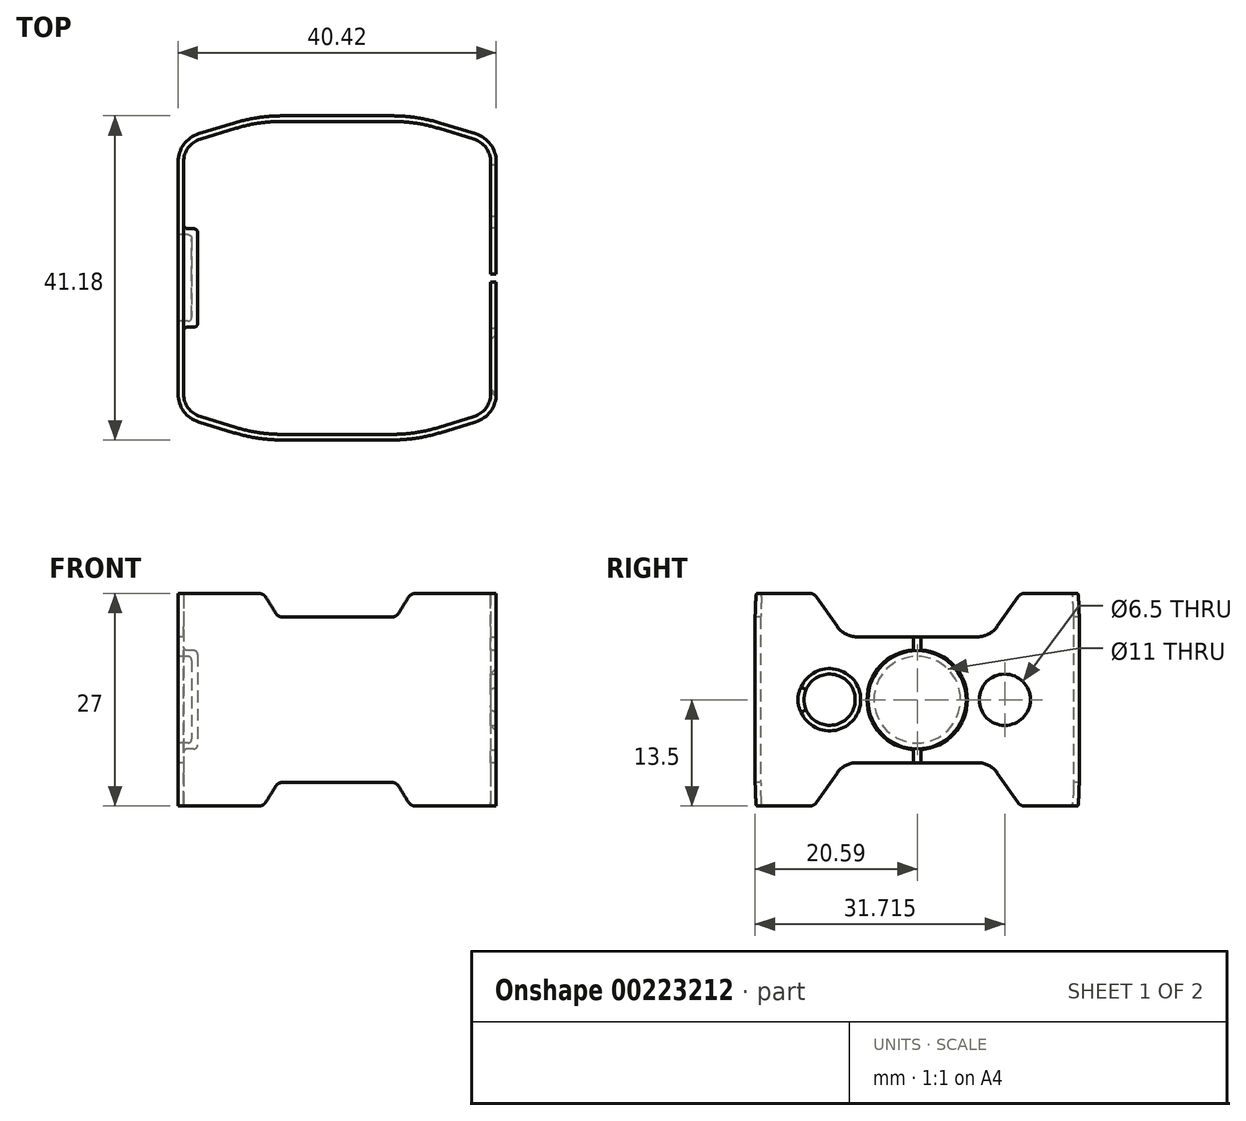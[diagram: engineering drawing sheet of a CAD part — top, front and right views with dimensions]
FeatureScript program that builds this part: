
annotation { "Feature Type Name" : "Feature", "Feature Type Description" : "" }
export const myFeature = defineFeature(function(context is Context, id is Id, definition is map)
    precondition{}
    {
        {
            var Q0;
            Q0=qCreatedBy(makeId("Top.planeOp"),FACE);
            var sketch = newSketch(context, id + "F0", { "sketchPlane" : qUnion([Q0])});
            skLineSegment(sketch, "E0", {"start": v(-19.5, 0) * mm, "end": v(-19.5, 14.75) * mm});
            skLineSegment(sketch, "E1", {"start": v(-17.38, 17.62) * mm, "end": v(-12.86, 19) * mm});
            skLineSegment(sketch, "E2", {"start": v(-7.01, 19.88) * mm, "end": v(0, 19.88) * mm});
            skLineSegment(sketch, "E3", {"start": v(0, 6.2) * mm, "end": v(0, -6.92) * mm, "construction": true});
            skLineSegment(sketch, "E4", {"start": v(0, -6.92) * mm, "end": v(-7.4, 0) * mm, "construction": true});
            skLineSegment(sketch, "E5", {"start": v(-7.4, 0) * mm, "end": v(6.12, 0) * mm, "construction": true});
            skPoint(sketch, "E6.visualSharp", {"position": v(-19.5, 16.97) * mm});
            skArc(sketch, "E6.filletArc", {"start": v(-17.38, 17.62) * mm, "mid": v(-18.91, 16.53) * mm, "end": v(-19.5, 14.75) * mm});
            skPoint(sketch, "E7.visualSharp", {"position": v(-10, 19.88) * mm});
            skArc(sketch, "E7.filletArc", {"start": v(-7.01, 19.88) * mm, "mid": v(-9.97, 19.66) * mm, "end": v(-12.86, 19) * mm});
            skLineSegment(sketch, "E8.MirrorCS", {"start": v(19.5, 0) * mm, "end": v(19.5, 14.75) * mm});
            skLineSegment(sketch, "E9.MirrorCS", {"start": v(17.38, 17.62) * mm, "end": v(12.86, 19) * mm});
            skLineSegment(sketch, "E10.MirrorCS", {"start": v(7.01, 19.88) * mm, "end": v(0, 19.88) * mm});
            skPoint(sketch, "E11.MirrorP", {"position": v(10, 19.88) * mm});
            skArc(sketch, "E12.MirrorCS", {"start": v(17.38, 17.62) * mm, "mid": v(18.91, 16.53) * mm, "end": v(19.5, 14.75) * mm});
            skArc(sketch, "E13.MirrorCS", {"start": v(7.01, 19.88) * mm, "mid": v(9.97, 19.66) * mm, "end": v(12.86, 19) * mm});
            skPoint(sketch, "E14.MirrorP", {"position": v(19.5, 16.97) * mm});
            skPoint(sketch, "E15.MirrorP", {"position": v(-19.5, -16.97) * mm});
            skPoint(sketch, "E16.MirrorP", {"position": v(-10, -19.88) * mm});
            skArc(sketch, "E17.MirrorCS", {"start": v(7.01, -19.88) * mm, "mid": v(9.97, -19.66) * mm, "end": v(12.86, -19) * mm});
            skArc(sketch, "E18.MirrorCS", {"start": v(17.38, -17.62) * mm, "mid": v(18.91, -16.53) * mm, "end": v(19.5, -14.75) * mm});
            skLineSegment(sketch, "E19.MirrorCS", {"start": v(7.01, -19.88) * mm, "end": v(0, -19.88) * mm});
            skLineSegment(sketch, "E20.MirrorCS", {"start": v(17.38, -17.62) * mm, "end": v(12.86, -19) * mm});
            skLineSegment(sketch, "E21.MirrorCS", {"start": v(19.5, 0) * mm, "end": v(19.5, -14.75) * mm});
            skArc(sketch, "E22.MirrorCS", {"start": v(-7.01, -19.88) * mm, "mid": v(-9.97, -19.66) * mm, "end": v(-12.86, -19) * mm});
            skArc(sketch, "E23.MirrorCS", {"start": v(-17.38, -17.62) * mm, "mid": v(-18.91, -16.53) * mm, "end": v(-19.5, -14.75) * mm});
            skPoint(sketch, "E24.MirrorP", {"position": v(10, -19.88) * mm});
            skLineSegment(sketch, "E25.MirrorCS", {"start": v(-19.5, 0) * mm, "end": v(-19.5, -14.75) * mm});
            skPoint(sketch, "E26.MirrorP", {"position": v(19.5, -16.97) * mm});
            skLineSegment(sketch, "E27.MirrorCS", {"start": v(-17.38, -17.62) * mm, "end": v(-12.86, -19) * mm});
            skLineSegment(sketch, "E28.MirrorCS", {"start": v(-7.01, -19.88) * mm, "end": v(0, -19.88) * mm});
            skLineSegment(sketch, "E29.0", {"start": v(20.21, -14.75) * mm, "end": v(20.21, 14.75) * mm});
            skArc(sketch, "E29.1", {"start": v(17.59, 18.3) * mm, "mid": v(19.48, 16.96) * mm, "end": v(20.21, 14.75) * mm});
            skLineSegment(sketch, "E29.2", {"start": v(17.59, 18.3) * mm, "end": v(13.07, 19.68) * mm});
            skArc(sketch, "E29.3", {"start": v(7.01, 20.59) * mm, "mid": v(10.07, 20.36) * mm, "end": v(13.07, 19.68) * mm});
            skLineSegment(sketch, "E29.4", {"start": v(7.01, 20.59) * mm, "end": v(0, 20.59) * mm});
            skLineSegment(sketch, "E29.5", {"start": v(-7.01, 20.59) * mm, "end": v(0, 20.59) * mm});
            skLineSegment(sketch, "E29.6", {"start": v(-20.21, -14.75) * mm, "end": v(-20.21, 14.75) * mm});
            skArc(sketch, "E29.7", {"start": v(-17.59, 18.3) * mm, "mid": v(-19.48, 16.96) * mm, "end": v(-20.21, 14.75) * mm});
            skLineSegment(sketch, "E29.8", {"start": v(-17.59, 18.3) * mm, "end": v(-13.07, 19.68) * mm});
            skArc(sketch, "E29.9", {"start": v(-7.01, 20.59) * mm, "mid": v(-10.07, 20.36) * mm, "end": v(-13.07, 19.68) * mm});
            skArc(sketch, "E30.1", {"start": v(-17.59, -18.3) * mm, "mid": v(-19.48, -16.96) * mm, "end": v(-20.21, -14.75) * mm});
            skLineSegment(sketch, "E30.2", {"start": v(-17.59, -18.3) * mm, "end": v(-13.07, -19.68) * mm});
            skArc(sketch, "E30.3", {"start": v(-7.01, -20.59) * mm, "mid": v(-10.07, -20.36) * mm, "end": v(-13.07, -19.68) * mm});
            skLineSegment(sketch, "E30.4", {"start": v(-7.01, -20.59) * mm, "end": v(0, -20.59) * mm});
            skLineSegment(sketch, "E30.5", {"start": v(7.01, -20.59) * mm, "end": v(0, -20.59) * mm});
            skArc(sketch, "E30.7", {"start": v(17.59, -18.3) * mm, "mid": v(19.48, -16.96) * mm, "end": v(20.21, -14.75) * mm});
            skLineSegment(sketch, "E30.8", {"start": v(17.59, -18.3) * mm, "end": v(13.07, -19.68) * mm});
            skArc(sketch, "E30.9", {"start": v(7.01, -20.59) * mm, "mid": v(10.07, -20.36) * mm, "end": v(13.07, -19.68) * mm});
            skSolve(sketch);
        }
        {
            var Q0;
            Q0 = qSketchRegion(id + "F0", true);
            extrude(context, id + "F1", {"entities" : qUnion([Q0]), "endBound" : BoundingType.SYMMETRIC, "depth" : 27 * mm});
        }
        {
            var Q0;
            Q0=makeQuery(id+"F1.opExtrude","SWEPT_FACE",FACE,{"disambiguationData":[OSD([sQuery(id+"F0.wireOp",EDGE,"E29.6")])]});
            var sketch = newSketch(context, id + "F2", { "sketchPlane" : qUnion([Q0])});
            skLineSegment(sketch, "E31", {"start": v(-12.86, 0) * mm, "end": v(13.63, 0) * mm, "construction": true});
            skLineSegment(sketch, "E32", {"start": v(0, 0) * mm, "end": v(0, 3.36) * mm, "construction": true});
            skLineSegment(sketch, "E33", {"start": v(0, 8) * mm, "end": v(-7.69, 8) * mm});
            skLineSegment(sketch, "E34", {"start": v(-10.15, 9.28) * mm, "end": v(-12.8, 13.07) * mm});
            skLineSegment(sketch, "E35", {"start": v(13.62, 13.5) * mm, "end": v(-13.62, 13.5) * mm});
            skPoint(sketch, "E36.visualSharp", {"position": v(-9.25, 8) * mm});
            skArc(sketch, "E36.filletArc", {"start": v(-10.15, 9.28) * mm, "mid": v(-9.07, 8.34) * mm, "end": v(-7.69, 8) * mm});
            skPoint(sketch, "E37.visualSharp", {"position": v(-13.1, 13.5) * mm});
            skArc(sketch, "E37.filletArc", {"start": v(-12.8, 13.07) * mm, "mid": v(-13.16, 13.39) * mm, "end": v(-13.62, 13.5) * mm});
            skArc(sketch, "E38.MirrorCS", {"start": v(12.8, 13.07) * mm, "mid": v(13.16, 13.39) * mm, "end": v(13.62, 13.5) * mm});
            skArc(sketch, "E39.MirrorCS", {"start": v(10.15, 9.28) * mm, "mid": v(9.07, 8.34) * mm, "end": v(7.69, 8) * mm});
            skPoint(sketch, "E40.MirrorP", {"position": v(13.1, 13.5) * mm});
            skLineSegment(sketch, "E41.MirrorCS", {"start": v(10.15, 9.28) * mm, "end": v(12.8, 13.07) * mm});
            skPoint(sketch, "E42.MirrorP", {"position": v(9.25, 8) * mm});
            skLineSegment(sketch, "E43.MirrorCS", {"start": v(0, 8) * mm, "end": v(7.69, 8) * mm});
            skArc(sketch, "E44.MirrorCS", {"start": v(10.15, -9.28) * mm, "mid": v(9.07, -8.34) * mm, "end": v(7.69, -8) * mm});
            skArc(sketch, "E45.MirrorCS", {"start": v(-12.8, -13.07) * mm, "mid": v(-13.16, -13.39) * mm, "end": v(-13.62, -13.5) * mm});
            skArc(sketch, "E46.MirrorCS", {"start": v(12.8, -13.07) * mm, "mid": v(13.16, -13.39) * mm, "end": v(13.62, -13.5) * mm});
            skArc(sketch, "E47.MirrorCS", {"start": v(-10.15, -9.28) * mm, "mid": v(-9.07, -8.34) * mm, "end": v(-7.69, -8) * mm});
            skPoint(sketch, "E48.MirrorP", {"position": v(-13.1, -13.5) * mm});
            skLineSegment(sketch, "E49.MirrorCS", {"start": v(-10.15, -9.28) * mm, "end": v(-12.8, -13.07) * mm});
            skLineSegment(sketch, "E50.MirrorCS", {"start": v(0, -8) * mm, "end": v(7.69, -8) * mm});
            skLineSegment(sketch, "E51.MirrorCS", {"start": v(10.15, -9.28) * mm, "end": v(12.8, -13.07) * mm});
            skPoint(sketch, "E52.MirrorP", {"position": v(-9.25, -8) * mm});
            skLineSegment(sketch, "E53.MirrorCS", {"start": v(0, -8) * mm, "end": v(-7.69, -8) * mm});
            skPoint(sketch, "E54.MirrorP", {"position": v(13.1, -13.5) * mm});
            skPoint(sketch, "E55.MirrorP", {"position": v(9.25, -8) * mm});
            skLineSegment(sketch, "E56.MirrorCS", {"start": v(13.62, -13.5) * mm, "end": v(-13.62, -13.5) * mm});
            skSolve(sketch);
        }
        {
            var Q0;
            Q0 = qSketchRegion(id + "F2", true);
            extrude(context, id + "F3", {"entities" : qUnion([Q0]), "operationType" : NewBodyOperationType.REMOVE, "endBound" : BoundingType.THROUGH_ALL, "oppositeDirection" : true, "depth" : 25 * mm});
        }
        {
            var Q0;
            Q0=makeQuery(id+"F1.opExtrude","SWEPT_FACE",FACE,{"disambiguationData":[OSD([sQuery(id+"F0.wireOp",EDGE,"E30.4"),sQuery(id+"F0.wireOp",EDGE,"E30.5")])]});
            var sketch = newSketch(context, id + "F4", { "sketchPlane" : qUnion([Q0])});
            skLineSegment(sketch, "E57", {"start": v(0, 0) * mm, "end": v(0, 3.35) * mm, "construction": true});
            skLineSegment(sketch, "E58", {"start": v(0, 3.35) * mm, "end": v(-3.06, 0) * mm, "construction": true});
            skLineSegment(sketch, "E59", {"start": v(-3.06, 0) * mm, "end": v(2.81, 0) * mm, "construction": true});
            skLineSegment(sketch, "E60", {"start": v(0, 10.5) * mm, "end": v(-6.94, 10.5) * mm});
            skLineSegment(sketch, "E61", {"start": v(-7.8, 10.97) * mm, "end": v(-9.06, 13.03) * mm});
            skLineSegment(sketch, "E62", {"start": v(9.91, 13.5) * mm, "end": v(-9.91, 13.5) * mm});
            skPoint(sketch, "E63.visualSharp", {"position": v(-7.5, 10.5) * mm});
            skArc(sketch, "E63.filletArc", {"start": v(-7.8, 10.97) * mm, "mid": v(-7.43, 10.63) * mm, "end": v(-6.94, 10.5) * mm});
            skPoint(sketch, "E64.visualSharp", {"position": v(-9.35, 13.5) * mm});
            skArc(sketch, "E64.filletArc", {"start": v(-9.06, 13.03) * mm, "mid": v(-9.42, 13.37) * mm, "end": v(-9.91, 13.5) * mm});
            skArc(sketch, "E65.MirrorCS", {"start": v(7.8, 10.97) * mm, "mid": v(7.43, 10.63) * mm, "end": v(6.94, 10.5) * mm});
            skArc(sketch, "E66.MirrorCS", {"start": v(9.06, 13.03) * mm, "mid": v(9.42, 13.37) * mm, "end": v(9.91, 13.5) * mm});
            skLineSegment(sketch, "E67.MirrorCS", {"start": v(7.8, 10.97) * mm, "end": v(9.06, 13.03) * mm});
            skPoint(sketch, "E68.MirrorP", {"position": v(7.5, 10.5) * mm});
            skLineSegment(sketch, "E69.MirrorCS", {"start": v(0, 10.5) * mm, "end": v(6.94, 10.5) * mm});
            skPoint(sketch, "E70.MirrorP", {"position": v(9.35, 13.5) * mm});
            skArc(sketch, "E71.MirrorCS", {"start": v(9.06, -13.03) * mm, "mid": v(9.42, -13.37) * mm, "end": v(9.91, -13.5) * mm});
            skArc(sketch, "E72.MirrorCS", {"start": v(-9.06, -13.03) * mm, "mid": v(-9.42, -13.37) * mm, "end": v(-9.91, -13.5) * mm});
            skArc(sketch, "E73.MirrorCS", {"start": v(-7.8, -10.97) * mm, "mid": v(-7.43, -10.63) * mm, "end": v(-6.94, -10.5) * mm});
            skArc(sketch, "E74.MirrorCS", {"start": v(7.8, -10.97) * mm, "mid": v(7.43, -10.63) * mm, "end": v(6.94, -10.5) * mm});
            skPoint(sketch, "E75.MirrorP", {"position": v(9.35, -13.5) * mm});
            skLineSegment(sketch, "E76.MirrorCS", {"start": v(-7.8, -10.97) * mm, "end": v(-9.06, -13.03) * mm});
            skLineSegment(sketch, "E77.MirrorCS", {"start": v(0, -10.5) * mm, "end": v(6.94, -10.5) * mm});
            skLineSegment(sketch, "E78.MirrorCS", {"start": v(9.91, -13.5) * mm, "end": v(-9.91, -13.5) * mm});
            skPoint(sketch, "E79.MirrorP", {"position": v(-9.35, -13.5) * mm});
            skLineSegment(sketch, "E80.MirrorCS", {"start": v(7.8, -10.97) * mm, "end": v(9.06, -13.03) * mm});
            skLineSegment(sketch, "E81.MirrorCS", {"start": v(0, -10.5) * mm, "end": v(-6.94, -10.5) * mm});
            skPoint(sketch, "E82.MirrorP", {"position": v(7.5, -10.5) * mm});
            skPoint(sketch, "E83.MirrorP", {"position": v(-7.5, -10.5) * mm});
            skSolve(sketch);
        }
        {
            var Q0;
            Q0 = qSketchRegion(id + "F4", true);
            extrude(context, id + "F5", {"entities" : qUnion([Q0]), "operationType" : NewBodyOperationType.REMOVE, "endBound" : BoundingType.THROUGH_ALL, "oppositeDirection" : true, "depth" : 25 * mm});
        }
        {
            var Q0;
            Q0=makeQuery(id+"F1.opExtrude","SWEPT_FACE",FACE,{"disambiguationData":[OSD([sQuery(id+"F0.wireOp",EDGE,"E29.0")])]});
            var sketch = newSketch(context, id + "F6", { "sketchPlane" : qUnion([Q0])});
            skLineSegment(sketch, "E84.bottom", {"start": v(0.5, 15) * mm, "end": v(-0.5, 15) * mm});
            skLineSegment(sketch, "E84.top", {"start": v(0.5, -15) * mm, "end": v(-0.5, -15) * mm});
            skLineSegment(sketch, "E84.left", {"start": v(0.5, 15) * mm, "end": v(0.5, -15) * mm});
            skLineSegment(sketch, "E84.right", {"start": v(-0.5, 15) * mm, "end": v(-0.5, -15) * mm});
            skPoint(sketch, "E84.middle", {"position": v(0, 0) * mm});
            skCircle(sketch, "E85", {"center": v(0, 0) * mm, "radius": 6.38 * mm});
            skCircle(sketch, "E86", {"center": v(-11.12, 0) * mm, "radius": 3.25 * mm});
            skLineSegment(sketch, "E87", {"start": v(0, 0) * mm, "end": v(0, 3.8) * mm, "construction": true});
            skCircle(sketch, "E88.MirrorC", {"center": v(11.12, 0) * mm, "radius": 3.25 * mm});
            skSolve(sketch);
        }
        {
            var Q0;
            Q0 = qSketchRegion(id + "F6", true);
            extrude(context, id + "F7", {"entities" : qUnion([Q0]), "operationType" : NewBodyOperationType.REMOVE, "oppositeDirection" : true, "depth" : 5 * mm});
        }
        {
            var Q0;
            Q0=makeQuery(id+"F7.boolean.opBoolean","COPY",EDGE,{"derivedFrom":makeQuery(id+"F7.opExtrude","CAP_EDGE",EDGE,{"disambiguationData":[OSD([sQuery(id+"F6.wireOp",EDGE,"E86")])],"isStart":true})});
            var Q1;
            Q1=makeQuery(id+"F7.boolean.opBoolean","COPY",EDGE,{"derivedFrom":makeQuery(id+"F7.opExtrude","CAP_EDGE",EDGE,{"disambiguationData":[OSD([sQuery(id+"F6.wireOp",EDGE,"E88.MirrorC")])],"isStart":true})});
            chamfer(context, id + "F8", {"entities" : qUnion([Q0, Q1]), "width" : .7 * mm, "tangentPropagation" : true});
        }
        {
            var Q0;
            Q0=makeQuery(id+"F1.opExtrude","SWEPT_FACE",FACE,{"disambiguationData":[OSD([sQuery(id+"F0.wireOp",EDGE,"E29.6")])]});
            var sketch = newSketch(context, id + "F9", { "sketchPlane" : qUnion([Q0])});
            skCircle(sketch, "E89", {"center": v(0, 0) * mm, "radius": 6.25 * mm});
            skSolve(sketch);
        }
        {
            var Q0;
            Q0=makeQuery(id+"F9.imprint","IMPRINT",FACE,{"disambiguationData":[TD([[makeQuery(id+"F9.imprint","IMPRINT",EDGE,{"derivedFrom":sQuery(id+"F9.wireOp",EDGE,"E89")}),1.0]])]});
            extrude(context, id + "F10", {"entities" : qUnion([Q0]), "operationType" : NewBodyOperationType.ADD, "oppositeDirection" : true, "depth" : 2.5 * mm});
        }
        {
            var Q0;
            Q0=makeQuery(id+"F1.opExtrude","SWEPT_FACE",FACE,{"disambiguationData":[OSD([sQuery(id+"F0.wireOp",EDGE,"E29.6")])]});
            var sketch = newSketch(context, id + "F11", { "sketchPlane" : qUnion([Q0])});
            skCircle(sketch, "E90", {"center": v(0, 0) * mm, "radius": 5.5 * mm});
            skSolve(sketch);
        }
        {
            var Q0;
            Q0 = qSketchRegion(id + "F11", true);
            extrude(context, id + "F12", {"entities" : qUnion([Q0]), "operationType" : NewBodyOperationType.REMOVE, "oppositeDirection" : true, "depth" : 1.75 * mm});
        }
        {
            var Q0;
            Q0=makeQuery(id+"F12.boolean.opBoolean","COPY",EDGE,{"derivedFrom":makeQuery(id+"F12.opExtrude","CAP_EDGE",EDGE,{"disambiguationData":[OSD([sQuery(id+"F11.wireOp",EDGE,"E90")])],"isStart":true})});
            var Q1;
            Q1=makeQuery(id+"F12.boolean.opBoolean","COPY",EDGE,{"derivedFrom":makeQuery(id+"F12.opExtrude","CAP_EDGE",EDGE,{"disambiguationData":[OSD([sQuery(id+"F11.wireOp",EDGE,"E90")])],"isStart":false})});
            fillet(context, id + "F13", {"entities" : qUnion([Q0, Q1]), "radius" : .5 * mm, "tangentPropagation" : true, "allowEdgeOverflow" : false});
        }
        {
            var Q0;
            Q0=makeQuery(id+"F10.boolean.opBoolean","INTERSECT",EDGE,{"derivedFrom":[makeQuery(id+"F1.opExtrude","SWEPT_FACE",FACE,{"disambiguationData":[OSD([sQuery(id+"F0.wireOp",EDGE,"E0"),sQuery(id+"F0.wireOp",EDGE,"E25.MirrorCS")])]}),makeQuery(id+"F10.opExtrude","SWEPT_FACE",FACE,{"disambiguationData":[OSD([sQuery(id+"F9.wireOp",EDGE,"E89")])]})]});
            var Q1;
            Q1=makeQuery(id+"F10.opExtrude","CAP_EDGE",EDGE,{"disambiguationData":[OSD([sQuery(id+"F9.wireOp",EDGE,"E89")])],"isStart":false});
            fillet(context, id + "F14", {"entities" : qUnion([Q0, Q1]), "radius" : .5 * mm, "tangentPropagation" : true, "allowEdgeOverflow" : false});
        }
    });
